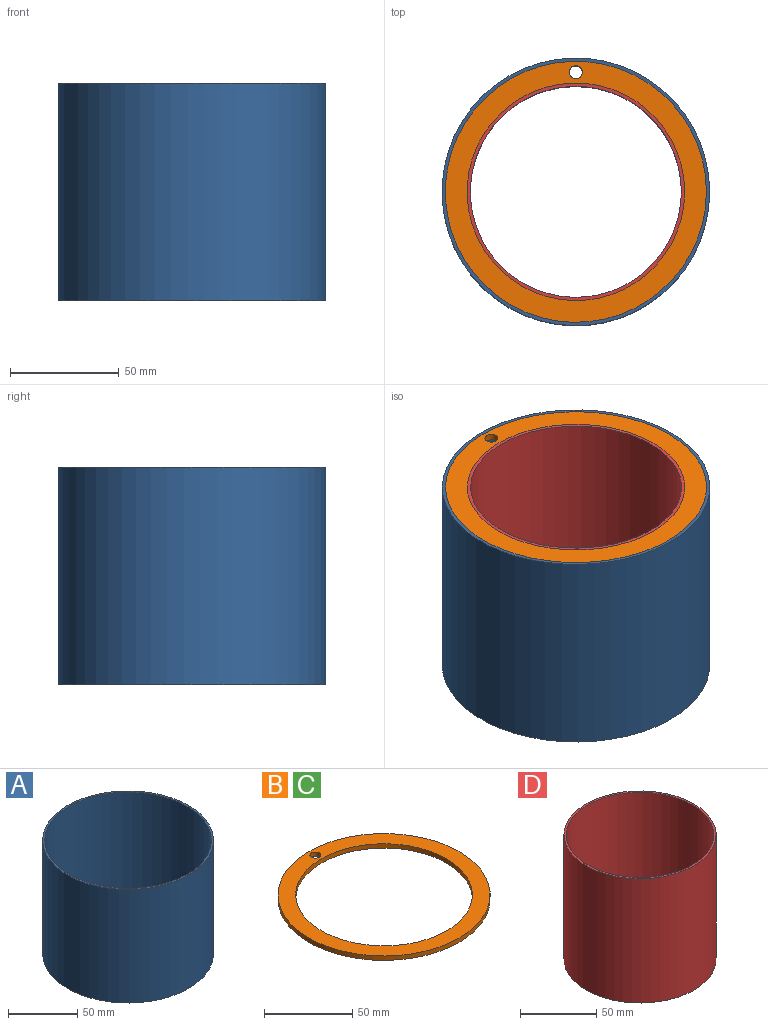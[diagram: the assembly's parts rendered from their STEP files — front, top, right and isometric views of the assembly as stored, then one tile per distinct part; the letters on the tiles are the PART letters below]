
ASSEMBLY  parts=4 mates=8
PART A: 4 faces, bbox 123x123x100 mm
  f0: cylinder r=60mm len=120mm, axis (0,0,-1), area 37699.1mm2, adj f2,f3
  f1: cylinder r=61.5mm len=123mm, axis (0,0,-1), area 38641.6mm2, adj f2,f3
  f2: plane 123x123mm, normal (0,0,1), area 572.6mm2, adj f0,f1
  f3: plane 123x123mm, normal (0,0,-1), area 572.6mm2, adj f0,f1
PART B: 5 faces, bbox 120x120x3 mm
  f0: cylinder r=3mm len=6mm, axis (0,0,-1), area 56.5mm2, adj f3,f4
  f1: cylinder r=50mm len=100mm, axis (0,0,-1), area 942.5mm2, adj f3,f4
  f2: cylinder r=60mm len=120mm, axis (0,0,-1), area 1131mm2, adj f3,f4
  f3: plane 120x120mm, normal (0,0,1), area 3427.5mm2, adj f0,f1,f2
  f4: plane 120x120mm, normal (0,0,-1), area 3427.5mm2, adj f0,f1,f2
PART C: same geometry as B
PART D: 4 faces, bbox 100x100x100 mm
  f0: cylinder r=48.5mm len=100mm, axis (0,0,-1), area 30473.4mm2, adj f2,f3
  f1: cylinder r=50mm len=100mm, axis (0,0,-1), area 31415.9mm2, adj f2,f3
  f2: plane 100x100mm, normal (0,0,1), area 464.2mm2, adj f0,f1
  f3: plane 100x100mm, normal (0,0,-1), area 464.2mm2, adj f0,f1
PLACE A t=(-24.35,-7.72,8.01)mm
PLACE B t=(-24.35,-7.72,105.01)mm
PLACE C t=(-24.35,-7.72,8.01)mm fixed
PLACE D t=(-24.35,-7.72,8.01)mm
MATE planar B.f3 <-> A.f1  axis (0,0,1) through (-24.35,-8.18,108.01)mm
MATE planar D.f1 <-> B.f3  axis (0,0,1) through (-24.35,-7.72,108.01)mm
MATE slider B.f0 <-> C.f0  axis (0,0,-1) through (-24.35,47.28,106.51)mm
MATE slider D.f1 <-> A.f1  axis (0,0,1) through (-24.35,-7.72,108.01)mm
MATE planar A.f1 <-> C.f4  axis (0,0,-1) through (-24.35,-7.72,8.01)mm
MATE slider D.f1 <-> B.f1  axis (0,0,-1) through (-24.35,-7.72,58.01)mm
MATE slider B.f1 <-> C.f1  axis (0,0,-1) through (-24.35,-7.72,106.51)mm
MATE slider A.f0 <-> C.f2  axis (0,0,-1) through (-24.35,-7.72,58.01)mm
